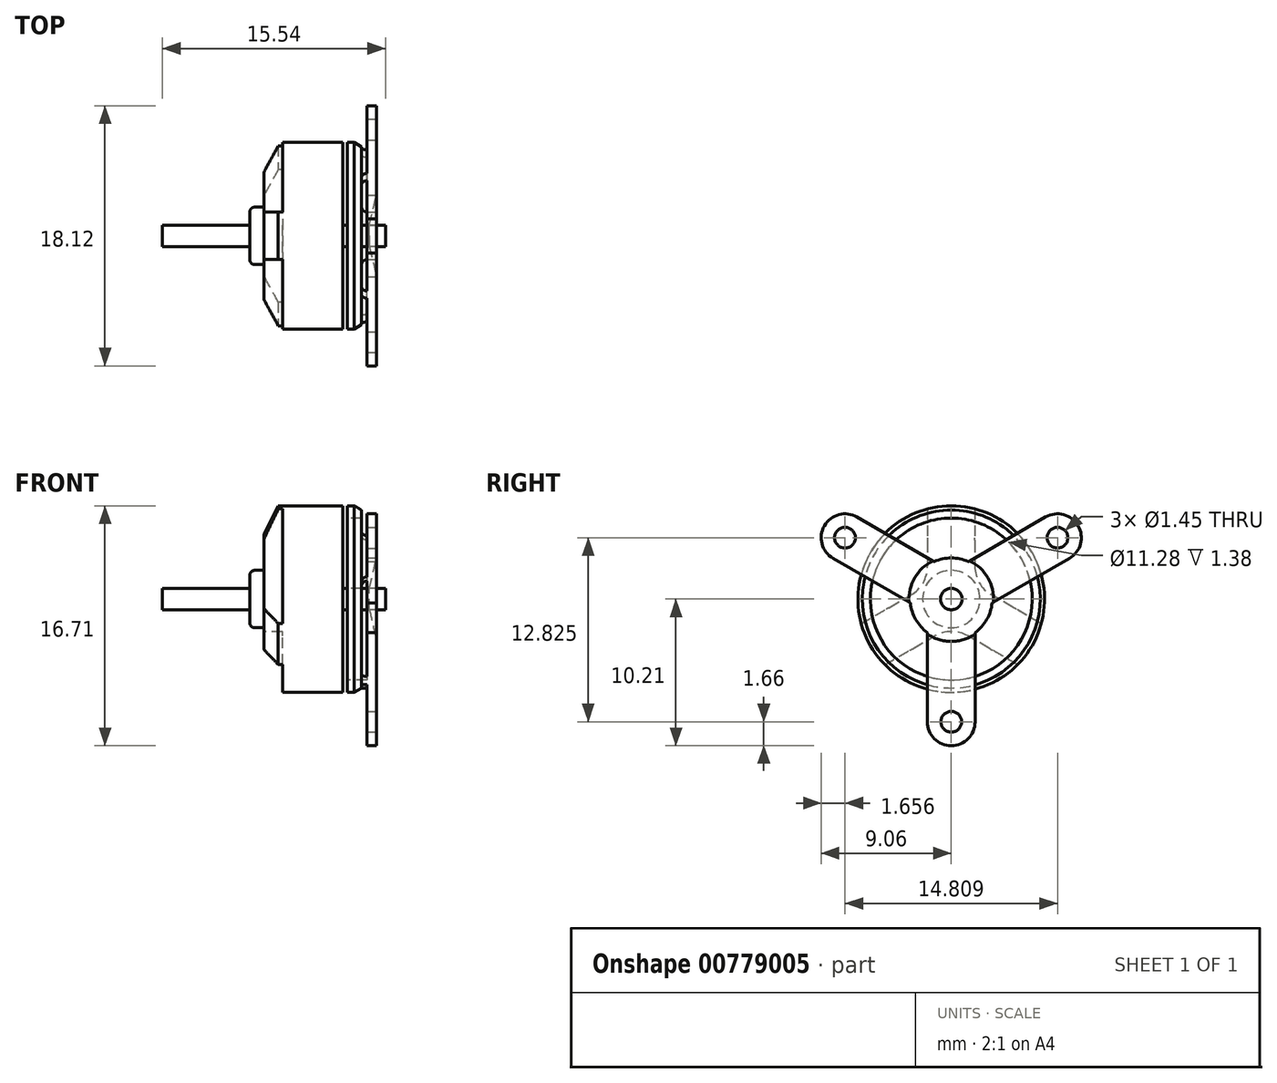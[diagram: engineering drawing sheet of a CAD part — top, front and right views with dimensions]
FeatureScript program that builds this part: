
annotation { "Feature Type Name" : "Feature", "Feature Type Description" : "" }
export const myFeature = defineFeature(function(context is Context, id is Id, definition is map)
    precondition{}
    {
        {
            var Q0;
            Q0=qCreatedBy(makeId("Front.planeOp"),FACE);
            var sketch = newSketch(context, id + "F0", { "sketchPlane" : qUnion([Q0])});
            skLineSegment(sketch, "E0", {"start": v(0, 0) * mm, "end": v(13.1, 0) * mm, "construction": true});
            skLineSegment(sketch, "E1", {"start": v(-14.92, 0) * mm, "end": v(-14.92, 0.75) * mm});
            skLineSegment(sketch, "E2", {"start": v(-14.92, 0.75) * mm, "end": v(0.62, 0.75) * mm});
            skLineSegment(sketch, "E3", {"start": v(0.62, 0.75) * mm, "end": v(0.62, 0) * mm});
            skLineSegment(sketch, "E4", {"start": v(-8.85, 0.75) * mm, "end": v(-8.85, 2) * mm});
            skLineSegment(sketch, "E5", {"start": v(-8.85, 2) * mm, "end": v(-7.85, 2) * mm});
            skLineSegment(sketch, "E6", {"start": v(-7.85, 2) * mm, "end": v(-7.85, 6.5) * mm});
            skLineSegment(sketch, "E7", {"start": v(-7.85, 6.5) * mm, "end": v(-2.35, 6.5) * mm});
            skLineSegment(sketch, "E8", {"start": v(-2.35, 6.5) * mm, "end": v(-2.35, 0.75) * mm});
            skLineSegment(sketch, "E9", {"start": v(-2.05, 6.5) * mm, "end": v(-1.55, 6.5) * mm});
            skLineSegment(sketch, "E10", {"start": v(-1.55, 6.5) * mm, "end": v(-1.05, 6.2) * mm});
            skLineSegment(sketch, "E11", {"start": v(-1.05, 6.2) * mm, "end": v(0, 6.2) * mm});
            skLineSegment(sketch, "E12", {"start": v(0, 6.2) * mm, "end": v(0, 0.75) * mm});
            skLineSegment(sketch, "E13", {"start": v(0.62, 0) * mm, "end": v(-14.92, 0) * mm});
            skLineSegment(sketch, "E14", {"start": v(-2.05, 5.64) * mm, "end": v(-0.67, 5.64) * mm});
            skLineSegment(sketch, "E15", {"start": v(-0.67, 5.64) * mm, "end": v(-0.67, 0.75) * mm});
            skLineSegment(sketch, "E16", {"start": v(-2.05, 6.5) * mm, "end": v(-2.05, 5.64) * mm});
            skSolve(sketch);
        }
        {
            var Q0;
            {var subQ0=sQuery(id+"F0.wireOp",EDGE,"E4");Q0=makeQuery(id+"F0.imprint","IMPRINT",FACE,{"disambiguationData":[TD([[makeQuery(id+"F0.imprint","IMPRINT",EDGE,{"derivedFrom":subQ0}),-1.0]])]});}
            var Q1;
            Q1=makeQuery(id+"F0.imprint","IMPRINT",FACE,{"disambiguationData":[TD([[makeQuery(id+"F0.imprint","IMPRINT",EDGE,{"derivedFrom":sQuery(id+"F0.wireOp",EDGE,"E9")}),-1.0]])]});
            var Q2;
            Q2=sQuery(id+"F0.wireOp",EDGE,"E0");
            revolve(context, id + "F1", {"surfaceOperationType" : NewSurfaceOperationType.NEW, "entities" : qUnion([Q0, Q1]), "axis" : qUnion([Q2]), "revolveType" : RevolveType.FULL});
        }
        {
            var Q0;
            Q0=makeQuery(id+"F1.opRevolve","SWEPT_FACE",FACE,{"disambiguationData":[OSD([sQuery(id+"F0.wireOp",EDGE,"E6")])]});
            var sketch = newSketch(context, id + "F2", { "sketchPlane" : qUnion([Q0])});
            skLineSegment(sketch, "E17", {"start": v(0, 0) * mm, "end": v(0, 6.5) * mm, "construction": true});
            skLineSegment(sketch, "E18", {"start": v(-1.65, 6.29) * mm, "end": v(-1.65, 2.28) * mm});
            skLineSegment(sketch, "E19.MirrorCS", {"start": v(1.65, 6.29) * mm, "end": v(1.65, 2.28) * mm});
            skLineSegment(sketch, "E20.1.0", {"start": v(-6.27, -1.71) * mm, "end": v(-2.8, 0.29) * mm});
            skLineSegment(sketch, "E20.1.1", {"start": v(-4.62, -4.57) * mm, "end": v(-1.15, -2.57) * mm});
            skLineSegment(sketch, "E20.2.0", {"start": v(4.62, -4.57) * mm, "end": v(1.15, -2.57) * mm});
            skLineSegment(sketch, "E20.2.1", {"start": v(6.27, -1.71) * mm, "end": v(2.8, 0.29) * mm});
            skPoint(sketch, "E20.center", {"position": v(0, 0) * mm});
            skArc(sketch, "E21", {"start": v(-1.65, 2.28) * mm, "mid": v(-1.96, 1.13) * mm, "end": v(-2.8, 0.29) * mm});
            skArc(sketch, "E22", {"start": v(2.8, 0.29) * mm, "mid": v(1.96, 1.13) * mm, "end": v(1.65, 2.28) * mm});
            skArc(sketch, "E23", {"start": v(1.15, -2.57) * mm, "mid": v(0, -2.26) * mm, "end": v(-1.15, -2.57) * mm});
            skSolve(sketch);
        }
        {
            var Q0;
            Q0=makeQuery(id+"F1.opRevolve","SWEPT_EDGE",EDGE,{"disambiguationData":[OSD([sQuery(id+"F0.wireOp",EDGE,"E6"),sQuery(id+"F0.wireOp",EDGE,"E7")])]});
            chamfer(context, id + "F3", {"entities" : qUnion([Q0]), "chamferType" : ChamferType.TWO_OFFSETS, "width1" : 2 * mm, "oppositeDirection" : false, "width2" : 1 * mm, "tangentPropagation" : true});
        }
        {
            var Q0;
            {var subQ0=sQuery(id+"F2.wireOp",EDGE,"E18");Q0=makeQuery(id+"F2.imprint","IMPRINT",FACE,{"disambiguationData":[TD([[makeQuery(id+"F2.imprint","IMPRINT",EDGE,{"derivedFrom":subQ0}),-1.0]])]});}
            var Q1;
            {var subQ0=sQuery(id+"F2.wireOp",EDGE,"E19.MirrorCS");Q1=makeQuery(id+"F2.imprint","IMPRINT",FACE,{"disambiguationData":[TD([[makeQuery(id+"F2.imprint","IMPRINT",EDGE,{"derivedFrom":subQ0}),1.0]])]});}
            var Q2;
            {var subQ0=sQuery(id+"F2.wireOp",EDGE,"E20.1.1");Q2=makeQuery(id+"F2.imprint","IMPRINT",FACE,{"disambiguationData":[TD([[makeQuery(id+"F2.imprint","IMPRINT",EDGE,{"derivedFrom":subQ0}),-1.0]])]});}
            extrude(context, id + "F4", {"entities" : qUnion([Q0, Q1, Q2]), "operationType" : NewBodyOperationType.REMOVE, "oppositeDirection" : true, "depth" : 1.3 * mm, "offsetDistance" : 25 * mm});
        }
        {
            var Q0;
            Q0=makeQuery(id+"F1.opRevolve","SWEPT_FACE",FACE,{"disambiguationData":[OSD([sQuery(id+"F0.wireOp",EDGE,"E12")])]});
            var sketch = newSketch(context, id + "F5", { "sketchPlane" : qUnion([Q0])});
            skLineSegment(sketch, "E24", {"start": v(1.66, -5.97) * mm, "end": v(1.66, -2.33) * mm});
            skLineSegment(sketch, "E25.MirrorCS", {"start": v(-1.66, -5.97) * mm, "end": v(-1.66, -2.33) * mm});
            skLineSegment(sketch, "E26", {"start": v(1.66, -5.97) * mm, "end": v(1.66, -8.55) * mm});
            skLineSegment(sketch, "E27", {"start": v(1.66, -8.55) * mm, "end": v(-1.66, -8.55) * mm, "construction": true});
            skLineSegment(sketch, "E28", {"start": v(-1.66, -8.55) * mm, "end": v(-1.66, -5.97) * mm});
            skArc(sketch, "E29", {"start": v(1.66, -8.55) * mm, "mid": v(0, -10.21) * mm, "end": v(-1.66, -8.55) * mm});
            skCircle(sketch, "E30", {"center": v(0, -8.55) * mm, "radius": 0.72 * mm});
            skCircle(sketch, "E31", {"center": v(0, 0) * mm, "radius": 2.86 * mm});
            skLineSegment(sketch, "E32.1.0", {"start": v(6, 1.55) * mm, "end": v(2.85, -0.27) * mm});
            skLineSegment(sketch, "E32.1.1", {"start": v(4.34, 4.42) * mm, "end": v(1.19, 2.6) * mm});
            skLineSegment(sketch, "E32.1.2", {"start": v(4.34, 4.42) * mm, "end": v(6.57, 5.71) * mm});
            skLineSegment(sketch, "E32.1.3", {"start": v(8.23, 2.84) * mm, "end": v(6, 1.55) * mm});
            skArc(sketch, "E32.1.4", {"start": v(6.57, 5.71) * mm, "mid": v(8.84, 5.1) * mm, "end": v(8.23, 2.84) * mm});
            skCircle(sketch, "E32.1.5", {"center": v(7.4, 4.27) * mm, "radius": 0.72 * mm});
            skLineSegment(sketch, "E32.2.0", {"start": v(-4.34, 4.42) * mm, "end": v(-1.19, 2.6) * mm});
            skLineSegment(sketch, "E32.2.1", {"start": v(-6, 1.55) * mm, "end": v(-2.85, -0.27) * mm});
            skLineSegment(sketch, "E32.2.2", {"start": v(-6, 1.55) * mm, "end": v(-8.23, 2.84) * mm});
            skLineSegment(sketch, "E32.2.3", {"start": v(-6.57, 5.71) * mm, "end": v(-4.34, 4.42) * mm});
            skArc(sketch, "E32.2.4", {"start": v(-8.23, 2.84) * mm, "mid": v(-8.84, 5.1) * mm, "end": v(-6.57, 5.71) * mm});
            skCircle(sketch, "E32.2.5", {"center": v(-7.4, 4.28) * mm, "radius": 0.72 * mm});
            skSolve(sketch);
        }
        {
            var Q0;
            {var subQ0=sQuery(id+"F5.wireOp",EDGE,"E32.1.1");Q0=makeQuery(id+"F5.imprint","IMPRINT",FACE,{"disambiguationData":[TD([[makeQuery(id+"F5.imprint","IMPRINT",EDGE,{"derivedFrom":subQ0}),-1.0]])]});}
            var Q1;
            {var subQ0=sQuery(id+"F5.wireOp",EDGE,"E24");Q1=makeQuery(id+"F5.imprint","IMPRINT",FACE,{"disambiguationData":[TD([[makeQuery(id+"F5.imprint","IMPRINT",EDGE,{"derivedFrom":subQ0}),-1.0]])]});}
            var Q2;
            {var subQ0=sQuery(id+"F5.wireOp",EDGE,"E25.MirrorCS");Q2=makeQuery(id+"F5.imprint","IMPRINT",FACE,{"disambiguationData":[TD([[makeQuery(id+"F5.imprint","IMPRINT",EDGE,{"derivedFrom":subQ0}),1.0]])]});}
            extrude(context, id + "F6", {"entities" : qUnion([Q0, Q1, Q2]), "operationType" : NewBodyOperationType.REMOVE, "oppositeDirection" : true, "depth" : 1.05 * mm, "offsetDistance" : 25 * mm});
        }
        {
            var Q0;
            {var subQ1=sQuery(id+"F5.wireOp",EDGE,"E32.2.2");Q0=makeQuery(id+"F5.imprint","IMPRINT",FACE,{"disambiguationData":[TD([[makeQuery(id+"F5.imprint","IMPRINT",EDGE,{"derivedFrom":subQ1}),-1.0]])]});}
            var Q1;
            {var subQ1=sQuery(id+"F5.wireOp",EDGE,"E32.1.2");Q1=makeQuery(id+"F5.imprint","IMPRINT",FACE,{"disambiguationData":[TD([[makeQuery(id+"F5.imprint","IMPRINT",EDGE,{"derivedFrom":subQ1}),-1.0]])]});}
            var Q2;
            {var subQ1=sQuery(id+"F5.wireOp",EDGE,"E26");Q2=makeQuery(id+"F5.imprint","IMPRINT",FACE,{"disambiguationData":[TD([[makeQuery(id+"F5.imprint","IMPRINT",EDGE,{"derivedFrom":subQ1}),-1.0]])]});}
            extrude(context, id + "F7", {"entities" : qUnion([Q0, Q1, Q2]), "operationType" : NewBodyOperationType.ADD, "oppositeDirection" : true, "depth" : 0.67 * mm, "offsetDistance" : 25 * mm});
        }
        {
            var Q0;
            Q0=makeQuery(id+"F6.boolean.opBoolean","COPY",EDGE,{"derivedFrom":makeQuery(id+"F6.opExtrude","CAP_EDGE",EDGE,{"disambiguationData":[OSD([sQuery(id+"F5.wireOp",EDGE,"E32.2.1")])],"isStart":false})});
            var Q1;
            Q1=makeQuery(id+"F6.boolean.opBoolean","COPY",EDGE,{"derivedFrom":makeQuery(id+"F6.opExtrude","CAP_EDGE",EDGE,{"disambiguationData":[OSD([sQuery(id+"F5.wireOp",EDGE,"E32.2.0")])],"isStart":false})});
            var Q2;
            Q2=makeQuery(id+"F6.boolean.opBoolean","COPY",EDGE,{"derivedFrom":makeQuery(id+"F6.opExtrude","CAP_EDGE",EDGE,{"disambiguationData":[OSD([sQuery(id+"F5.wireOp",EDGE,"E32.1.1")])],"isStart":false})});
            var Q3;
            Q3=makeQuery(id+"F6.boolean.opBoolean","COPY",EDGE,{"derivedFrom":makeQuery(id+"F6.opExtrude","CAP_EDGE",EDGE,{"disambiguationData":[OSD([sQuery(id+"F5.wireOp",EDGE,"E32.1.0")])],"isStart":false})});
            var Q4;
            Q4=makeQuery(id+"F6.boolean.opBoolean","COPY",EDGE,{"derivedFrom":makeQuery(id+"F6.opExtrude","CAP_EDGE",EDGE,{"disambiguationData":[OSD([sQuery(id+"F5.wireOp",EDGE,"E24")])],"isStart":false})});
            var Q5;
            Q5=makeQuery(id+"F6.boolean.opBoolean","COPY",EDGE,{"derivedFrom":makeQuery(id+"F6.opExtrude","CAP_EDGE",EDGE,{"disambiguationData":[OSD([sQuery(id+"F5.wireOp",EDGE,"E25.MirrorCS")])],"isStart":false})});
            var Q6;
            {var subQ0=sQuery(id+"F0.wireOp",EDGE,"E6");var subQ1=makeQuery(id+"F1.opRevolve","SWEPT_FACE",FACE,{"disambiguationData":[OSD([subQ0])]});var subQ2=sQuery(id+"F0.wireOp",EDGE,"E7");Q6=makeQuery(id+"F4.boolean.opBoolean","SPLIT",EDGE,{"disambiguationData":[TD([makeQuery(id+"F4.opExtrude","SWEPT_FACE",FACE,{"disambiguationData":[OSD([sQuery(id+"F2.wireOp",EDGE,"E18")])]})])],"derivedFrom":makeQuery(id+"F3.opChamfer","BLEND_EDGE",EDGE,{"blendedFrom":[makeQuery(id+"F1.opRevolve","SWEPT_EDGE",EDGE,{"disambiguationData":[OSD([subQ0,subQ2])]}),subQ1],"blendedInto":[subQ1]})});}
            var Q7;
            {var subQ0=sQuery(id+"F0.wireOp",EDGE,"E6");var subQ1=makeQuery(id+"F1.opRevolve","SWEPT_FACE",FACE,{"disambiguationData":[OSD([subQ0])]});var subQ2=sQuery(id+"F0.wireOp",EDGE,"E7");Q7=makeQuery(id+"F4.boolean.opBoolean","SPLIT",EDGE,{"disambiguationData":[TD([makeQuery(id+"F4.opExtrude","SWEPT_FACE",FACE,{"disambiguationData":[OSD([sQuery(id+"F2.wireOp",EDGE,"E20.1.0")])]})])],"derivedFrom":makeQuery(id+"F3.opChamfer","BLEND_EDGE",EDGE,{"blendedFrom":[makeQuery(id+"F1.opRevolve","SWEPT_EDGE",EDGE,{"disambiguationData":[OSD([subQ0,subQ2])]}),subQ1],"blendedInto":[subQ1]})});}
            var Q8;
            {var subQ0=sQuery(id+"F0.wireOp",EDGE,"E6");var subQ1=makeQuery(id+"F1.opRevolve","SWEPT_FACE",FACE,{"disambiguationData":[OSD([subQ0])]});var subQ2=sQuery(id+"F0.wireOp",EDGE,"E7");Q8=makeQuery(id+"F4.boolean.opBoolean","SPLIT",EDGE,{"disambiguationData":[TD([makeQuery(id+"F4.opExtrude","SWEPT_FACE",FACE,{"disambiguationData":[OSD([sQuery(id+"F2.wireOp",EDGE,"E20.2.0")])]})])],"derivedFrom":makeQuery(id+"F3.opChamfer","BLEND_EDGE",EDGE,{"blendedFrom":[makeQuery(id+"F1.opRevolve","SWEPT_EDGE",EDGE,{"disambiguationData":[OSD([subQ0,subQ2])]}),subQ1],"blendedInto":[subQ1]})});}
            var Q9;
            Q9=makeQuery(id+"F1.opRevolve","SWEPT_EDGE",EDGE,{"disambiguationData":[OSD([sQuery(id+"F0.wireOp",EDGE,"E4"),sQuery(id+"F0.wireOp",EDGE,"E5")])]});
            fillet(context, id + "F8", {"entities" : qUnion([Q0, Q1, Q2, Q3, Q4, Q5, Q6, Q7, Q8, Q9]), "radius" : 0.36 * mm, "tangentPropagation" : true, "allowEdgeOverflow" : false});
        }
        {
            var Q0;
            Q0=makeQuery(id+"F1.opRevolve","SWEPT_EDGE",EDGE,{"disambiguationData":[OSD([sQuery(id+"F0.wireOp",EDGE,"E2"),sQuery(id+"F0.wireOp",EDGE,"E12")])]});
            chamfer(context, id + "F9", {"entities" : qUnion([Q0]), "chamferType" : ChamferType.TWO_OFFSETS, "width1" : 2.2 * mm, "oppositeDirection" : false, "width2" : .5 * mm, "tangentPropagation" : true});
        }
        {
            var Q0;
            {var subQ4=sQuery(id+"F0.wireOp",EDGE,"E1");Q0=makeQuery(id+"F0.imprint","IMPRINT",FACE,{"disambiguationData":[TD([[makeQuery(id+"F0.imprint","IMPRINT",EDGE,{"derivedFrom":subQ4}),-1.0]])]});}
            var Q1;
            Q1=sQuery(id+"F0.wireOp",EDGE,"E0");
            revolve(context, id + "F10", {"operationType" : NewBodyOperationType.ADD, "surfaceOperationType" : NewSurfaceOperationType.NEW, "entities" : qUnion([Q0]), "axis" : qUnion([Q1]), "revolveType" : RevolveType.FULL});
        }
    });
